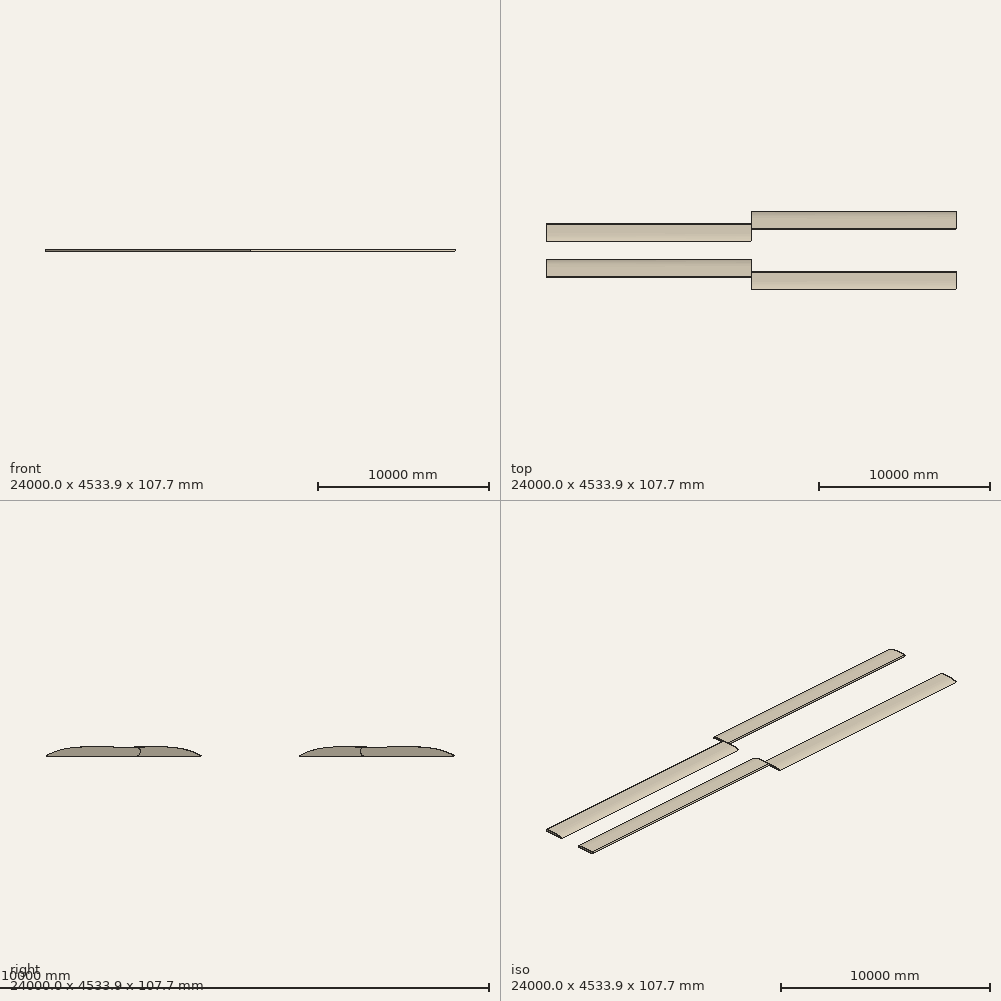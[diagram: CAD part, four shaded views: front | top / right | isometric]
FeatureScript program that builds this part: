
annotation { "Feature Type Name" : "Feature", "Feature Type Description" : "" }
export const myFeature = defineFeature(function(context is Context, id is Id, definition is map)
    precondition{}
    {
        {
            var Q0;
            Q0=qCreatedBy(makeId("Right.planeOp"),FACE);
            var sketch = newSketch(context, id + "F0", { "sketchPlane" : qUnion([Q0])});
            skLineSegment(sketch, "E0", {"start": v(-466.95, -100) * mm, "end": v(533.05, -100) * mm});
            skPoint(sketch, "E1", {"position": v(533.05, 0) * mm});
            skArc(sketch, "E2", {"start": v(533.05, -100) * mm, "mid": v(583.05, -50) * mm, "end": v(533.05, 0) * mm});
            skPoint(sketch, "E3", {"position": v(-132.85, 0) * mm});
            skFitSpline(sketch, "E4", {"points": [v(533.05, 0) * mm, v(-132.85, 0) * mm, v(-466.95, -100) * mm], "startDerivative": vector(-1264.65, 0) * mm, "endDerivative": vector(-695.63, -404.9) * mm});
            skSolve(sketch);
        }
        {
            var Q0;
            Q0=makeQuery(id+"F0.imprint","IMPRINT",FACE,{"disambiguationData":[TD([[makeQuery(id+"F0.imprint","IMPRINT",EDGE,{"derivedFrom":sQuery(id+"F0.wireOp",EDGE,"E0")}),1.0]])]});
            extrude(context, id + "F1", {"entities" : qUnion([Q0]), "oppositeDirection" : true, "depth" : 12000 * mm, "offsetDistance" : 25 * mm});
        }
        {
            var Q0;
            Q0=qCreatedBy(makeId("Front.planeOp"),FACE);
            var sketch = newSketch(context, id + "F2", { "sketchPlane" : qUnion([Q0])});
            skLineSegment(sketch, "E5", {"start": v(0, 58.66) * mm, "end": v(0, -86.39) * mm});
            skSolve(sketch);
        }
        {
            var Q0;
            Q0=makeQuery(id+"F1.opExtrude","SWEPT_BODY",BODY,{"disambiguationData":[OSD([sQuery(id+"F0.wireOp",EDGE,"E0"),sQuery(id+"F0.wireOp",EDGE,"E2"),sQuery(id+"F0.wireOp",EDGE,"E4")])]});
            var Q1;
            Q1=sQuery(id+"F2.wireOp",EDGE,"E5");
            transform(context, id + "F3", {"entities" : qUnion([Q0]), "transformType" : TransformType.ROTATION, "transformAxis" : qUnion([Q1]), "angle" : 180 * degree, "makeCopy" : true});
        }
        {
            var Q0;
            Q0=makeQuery(id+"F3.opPattern","COPY",BODY,{"derivedFrom":makeQuery(id+"F1.opExtrude","SWEPT_BODY",BODY,{"disambiguationData":[OSD([sQuery(id+"F0.wireOp",EDGE,"E0"),sQuery(id+"F0.wireOp",EDGE,"E2"),sQuery(id+"F0.wireOp",EDGE,"E4")])]}),"instanceName":"1"});
            transform(context, id + "F4", {"entities" : qUnion([Q0]), "transformType" : TransformType.TRANSLATION_3D, "dx" : 0 * mm, "dy" : 800 * mm, "dz" : 0 * mm, "makeCopy" : false});
        }
        {
            var Q0;
            Q0=makeQuery(id+"F1.opExtrude","SWEPT_BODY",BODY,{"disambiguationData":[OSD([sQuery(id+"F0.wireOp",EDGE,"E0"),sQuery(id+"F0.wireOp",EDGE,"E2"),sQuery(id+"F0.wireOp",EDGE,"E4")])]});
            var Q1;
            Q1=makeQuery(id+"F3.opPattern","COPY",BODY,{"derivedFrom":makeQuery(id+"F1.opExtrude","SWEPT_BODY",BODY,{"disambiguationData":[OSD([sQuery(id+"F0.wireOp",EDGE,"E0"),sQuery(id+"F0.wireOp",EDGE,"E2"),sQuery(id+"F0.wireOp",EDGE,"E4")])]}),"instanceName":"1"});
            booleanBodies(context, id + "F5", {"operationType" : BooleanOperationType.UNION, "tools" : qUnion([Q0, Q1])});
        }
        {
            var Q0;
            {var subQ0=makeQuery(id+"F1.opExtrude","SWEPT_FACE",FACE,{"disambiguationData":[OSD([sQuery(id+"F0.wireOp",EDGE,"E0")])]});Q0=makeQuery(id+"F5.opBoolean","MERGE",FACE,{"derivedFrom":[subQ0,makeQuery(id+"F3.opPattern","COPY",FACE,{"derivedFrom":subQ0,"instanceName":"1"})]});}
            var sketch = newSketch(context, id + "F6", { "sketchPlane" : qUnion([Q0])});
            skPoint(sketch, "E6", {"position": v(0, -400.75) * mm});
            skCircle(sketch, "E7", {"center": v(0, -400.75) * mm, "radius": 9.5 * mm});
            skSolve(sketch);
        }
        {
            var Q0;
            Q0=qSketchRegion(id+"F6",true);
            extrude(context, id + "F7", {"entities" : qUnion([Q0]), "operationType" : NewBodyOperationType.REMOVE, "oppositeDirection" : true, "depth" : 250 * mm, "offsetDistance" : 25 * mm});
        }
        {
            var Q0;
            {var subQ0=makeQuery(id+"F1.opExtrude","SWEPT_FACE",FACE,{"disambiguationData":[OSD([sQuery(id+"F0.wireOp",EDGE,"E0")])]});Q0=makeQuery(id+"F5.opBoolean","MERGE",FACE,{"derivedFrom":[subQ0,makeQuery(id+"F3.opPattern","COPY",FACE,{"derivedFrom":subQ0,"instanceName":"1"})]});}
            var sketch = newSketch(context, id + "F8", { "sketchPlane" : qUnion([Q0])});
            skCircle(sketch, "E8", {"center": v(0, -400.75) * mm, "radius": 10.5 * mm});
            skSolve(sketch);
        }
        {
            var Q0;
            Q0=qSketchRegion(id+"F8",true);
            extrude(context, id + "F9", {"entities" : qUnion([Q0]), "operationType" : NewBodyOperationType.REMOVE, "oppositeDirection" : true, "depth" : 20 * mm, "offsetDistance" : 25 * mm});
        }
        {
            var Q0;
            Q0=makeQuery(id+"F7.boolean.opBoolean","INTERSECT",EDGE,{"derivedFrom":[makeQuery(id+"F1.opExtrude","SWEPT_FACE",FACE,{"disambiguationData":[OSD([sQuery(id+"F0.wireOp",EDGE,"E4")])]}),makeQuery(id+"F7.opExtrude","SWEPT_FACE",FACE,{"disambiguationData":[OSD([sQuery(id+"F6.wireOp",EDGE,"E7")])]})]});
            cPoint(context, id + "F10", {"entities" : qUnion([Q0]), "parameter" : 0.5});
        }
        {
            var Q0;
            Q0=makeQuery(id+"F7.boolean.opBoolean","INTERSECT",EDGE,{"derivedFrom":[makeQuery(id+"F3.opPattern","COPY",FACE,{"derivedFrom":makeQuery(id+"F1.opExtrude","SWEPT_FACE",FACE,{"disambiguationData":[OSD([sQuery(id+"F0.wireOp",EDGE,"E4")])]}),"instanceName":"1"}),makeQuery(id+"F7.opExtrude","SWEPT_FACE",FACE,{"disambiguationData":[OSD([sQuery(id+"F6.wireOp",EDGE,"E7")])]})]});
            cPoint(context, id + "F11", {"entities" : qUnion([Q0]), "parameter" : 0.5});
        }
        {
            var Q0;
            Q0=qCreatedBy(id+"F10",VERTEX);
            var Q1;
            Q1=qCreatedBy(id+"F11",VERTEX);
            cPlane(context, id + "F12", {"entities" : qUnion([Q0, Q1]), "cplaneType" : CPlaneType.MID_PLANE, "offset" : 25 * mm, "width" : 150 * mm, "height" : 150 * mm});
        }
        {
            var Q0;
            Q0=qCreatedBy(id+"F12.planeOp",FACE);
            var sketch = newSketch(context, id + "F13", { "sketchPlane" : qUnion([Q0])});
            skLineSegment(sketch, "E9", {"start": v(410.28, 1.62) * mm, "end": v(410.28, 129.7) * mm});
            skSolve(sketch);
        }
        {
            var Q0;
            Q0=sQuery(id+"F13.wireOp",EDGE,"E9");
            var Q1;
            Q1=sQuery(id+"F13.wireOp",VERTEX,"E9.start");
            cPlane(context, id + "F14", {"entities" : qUnion([Q0, Q1]), "cplaneType" : CPlaneType.LINE_POINT, "offset" : 25 * mm, "width" : 150 * mm, "height" : 150 * mm});
        }
        {
            var Q0;
            Q0=qCreatedBy(id+"F14.planeOp",FACE);
            var sketch = newSketch(context, id + "F15", { "sketchPlane" : qUnion([Q0])});
            skCircle(sketch, "E10", {"center": v(-0.15, 400.75) * mm, "radius": 10.5 * mm});
            skSolve(sketch);
        }
        {
            var Q0;
            Q0=qSketchRegion(id+"F15",true);
            extrude(context, id + "F16", {"entities" : qUnion([Q0]), "operationType" : NewBodyOperationType.REMOVE, "oppositeDirection" : true, "depth" : 20 * mm, "offsetDistance" : 25 * mm});
        }
        {
            var Q0;
            Q0=qCreatedBy(makeId("Front.planeOp"),FACE);
            cPlane(context, id + "F17", {"entities" : qUnion([Q0]), "cplaneType" : CPlaneType.OFFSET, "offset" : 1000 * mm, "width" : 150 * mm, "height" : 150 * mm});
        }
        {
            var Q0;
            Q0=makeQuery(id+"F1.opExtrude","SWEPT_BODY",BODY,{"disambiguationData":[OSD([sQuery(id+"F0.wireOp",EDGE,"E0"),sQuery(id+"F0.wireOp",EDGE,"E2"),sQuery(id+"F0.wireOp",EDGE,"E4")])]});
            var Q1;
            Q1=qCreatedBy(id+"F17.planeOp",FACE);
            mirror(context, id + "F18", {"entities" : qUnion([Q0]), "mirrorPlane" : qUnion([Q1])});
        }
    });
